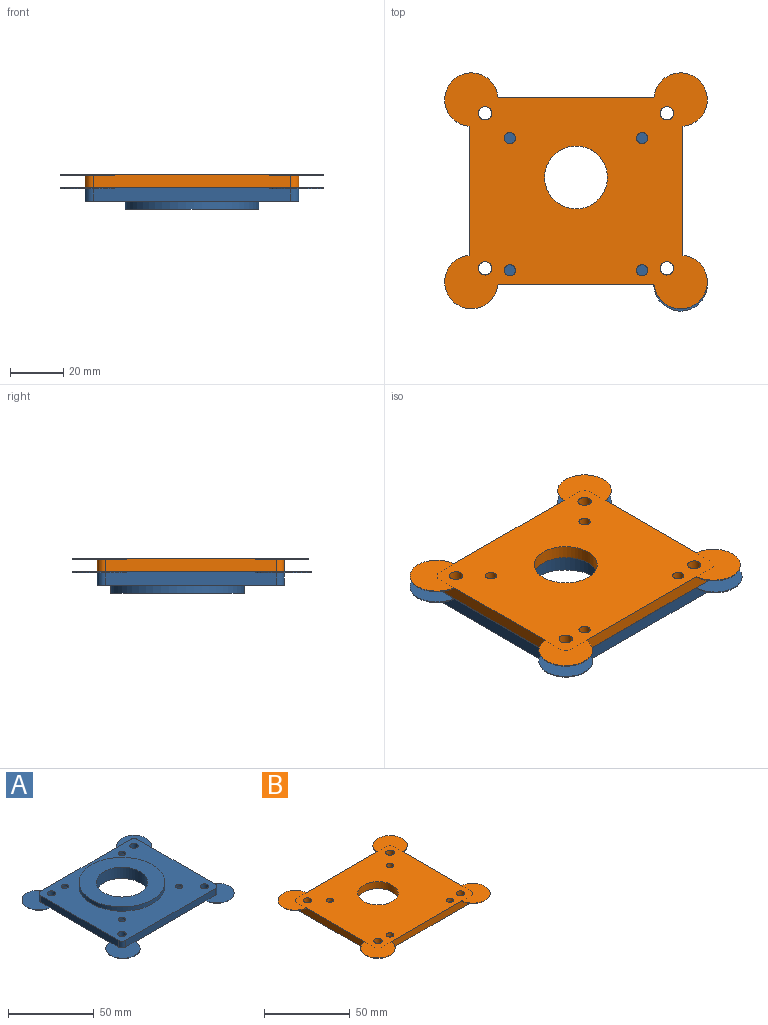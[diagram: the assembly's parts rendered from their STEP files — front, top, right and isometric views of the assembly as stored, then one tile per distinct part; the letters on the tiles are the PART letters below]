
ASSEMBLY  parts=2 mates=1
PART A: 37 faces, bbox 98.2x89.1x8 mm
  f0: cylinder r=3mm len=4.7mm, axis (0,0,-1), area 22.1mm2, adj f9,f10,f16,f36
  f1: cylinder r=3mm len=4.7mm, axis (0,0,1), area 22.1mm2, adj f8,f10,f16,f34
  f2: cylinder r=3mm len=4.7mm, axis (0,0,1), area 22.1mm2, adj f8,f10,f11,f32
  f3: cylinder r=3mm len=4.7mm, axis (0,0,-1), area 22.1mm2, adj f9,f10,f11,f30
  f4: cylinder r=2.1mm len=4.2mm, axis (0,0,1), area 21.1mm2, adj f10,f27
  f5: cylinder r=2.1mm len=4.2mm, axis (0,0,1), area 21.1mm2, adj f10,f28
  f6: cylinder r=2.1mm len=4.2mm, axis (0,0,1), area 21.1mm2, adj f10,f25
  f7: cylinder r=2.1mm len=4.2mm, axis (0,0,1), area 21.1mm2, adj f10,f26
  f8: plane 64x5mm, normal (1,0,0), area 315.3mm2, adj f1,f2,f10,f13,f31,f32,f33,f34
  f9: plane 64x5mm, normal (-1,0,0), area 315.6mm2, adj f0,f3,f10,f13,f29,f30,f35,f36
  f10: plane 80x70mm, normal (0,0,1), area 3494.8mm2, adj f0,f1,f2,f3,f4,f5,f6,f7
  f11: plane 74x5mm, normal (0,-1,0), area 365.3mm2, adj f2,f3,f10,f13,f29,f30,f31,f32
  f12: cylinder r=15mm len=30mm, axis (0,0,-1), area 754mm2, adj f13,f15
  f13: plane 98.24x89.12mm, normal (0,0,-1), area 5379.2mm2, adj f8,f9,f11,f12,f16,f17,f18,f19
  f14: cylinder r=25mm len=50mm, axis (0,0,-1), area 471.2mm2, adj f10,f15
  f15: plane 50x50mm, normal (0,0,1), area 1256.6mm2, adj f12,f14
  f16: plane 74x5mm, normal (0,1,0), area 365.3mm2, adj f0,f1,f10,f13,f33,f34,f35,f36
  f17: cylinder r=2.5mm len=5mm, axis (0,0,-1), area 78.5mm2, adj f10,f13
  f18: cylinder r=2.5mm len=5mm, axis (0,0,-1), area 78.5mm2, adj f10,f13
  f19: cylinder r=2.5mm len=5mm, axis (0,0,-1), area 78.5mm2, adj f10,f13
  f20: cylinder r=2.5mm len=5mm, axis (0,0,-1), area 78.5mm2, adj f10,f13
  f21: cylinder r=5mm len=10mm, axis (0,0,-1), area 15.7mm2, adj f13,f26
  f22: cylinder r=5mm len=10mm, axis (0,0,-1), area 15.7mm2, adj f13,f25
  f23: cylinder r=5mm len=10mm, axis (0,0,-1), area 15.7mm2, adj f13,f28
  f24: cylinder r=5mm len=10mm, axis (0,0,-1), area 15.7mm2, adj f13,f27
  f25: cone r=5.1mm half-angle=45deg, axis (0,0,-1), area 91.5mm2, adj f6,f22
  f26: cone r=5.1mm half-angle=45deg, axis (0,0,-1), area 91.5mm2, adj f7,f21
  f27: cone r=5.1mm half-angle=45deg, axis (0,0,-1), area 91.5mm2, adj f4,f24
  f28: cone r=5.1mm half-angle=45deg, axis (0,0,-1), area 91.5mm2, adj f5,f23
  f29: cylinder r=10mm len=20mm, axis (0,0,-1), area 13.9mm2, adj f9,f11,f13,f30
  f30: plane 20x19.96mm, normal (0,0,1), area 228.8mm2, adj f3,f9,f11,f29
  f31: cylinder r=10mm len=19.96mm, axis (0,0,-1), area 13.6mm2, adj f8,f11,f13,f32
  f32: plane 19.96x19.96mm, normal (0,0,1), area 219.2mm2, adj f2,f8,f11,f31
  f33: cylinder r=10mm len=19.96mm, axis (0,0,-1), area 13.6mm2, adj f8,f13,f16,f34
  f34: plane 19.96x19.96mm, normal (0,0,1), area 219.2mm2, adj f1,f8,f16,f33
  f35: cylinder r=10mm len=19.96mm, axis (0,0,-1), area 13.6mm2, adj f9,f13,f16,f36
  f36: plane 19.96x19.96mm, normal (0,0,1), area 219.2mm2, adj f0,f9,f16,f35
PART B: 35 faces, bbox 98.2x88.2x5 mm
  f0: cylinder r=3mm len=4.7mm, axis (0,0,1), area 22.1mm2, adj f9,f11,f14,f34
  f1: cylinder r=3mm len=4.7mm, axis (0,0,-1), area 22.1mm2, adj f8,f11,f14,f32
  f2: cylinder r=3mm len=4.7mm, axis (0,0,-1), area 22.1mm2, adj f8,f11,f12,f30
  f3: cylinder r=3mm len=4.7mm, axis (0,0,1), area 22.1mm2, adj f9,f11,f12,f28
  f4: cylinder r=2.1mm len=4.2mm, axis (0,0,-1), area 34.3mm2, adj f10,f25
  f5: cylinder r=2.1mm len=4.2mm, axis (0,0,-1), area 34.3mm2, adj f10,f23
  f6: cylinder r=2.1mm len=4.2mm, axis (0,0,-1), area 34.3mm2, adj f10,f26
  f7: cylinder r=2.1mm len=4.2mm, axis (0,0,-1), area 34.3mm2, adj f10,f24
  f8: plane 64x5mm, normal (1,0,0), area 315.3mm2, adj f1,f2,f10,f11,f29,f30,f31,f32
  f9: plane 64x5mm, normal (-1,0,0), area 315.3mm2, adj f0,f3,f10,f11,f27,f28,f33,f34
  f10: plane 98.24x88.24mm, normal (0,0,1), area 5901.5mm2, adj f4,f5,f6,f7,f8,f9,f12,f13
  f11: plane 80x70mm, normal (0,0,-1), area 4878.9mm2, adj f0,f1,f2,f3,f8,f9,f12,f13
  f12: plane 74x5mm, normal (0,1,0), area 365.3mm2, adj f2,f3,f10,f11,f27,f28,f29,f30
  f13: cylinder r=11.75mm len=23.5mm, axis (0,0,-1), area 369.1mm2, adj f10,f11
  f14: plane 74x5mm, normal (0,-1,0), area 365.3mm2, adj f0,f1,f10,f11,f31,f32,f33,f34
  f15: cylinder r=2.5mm len=5mm, axis (0,0,-1), area 78.5mm2, adj f10,f11
  f16: cylinder r=2.5mm len=5mm, axis (0,0,-1), area 78.5mm2, adj f10,f11
  f17: cylinder r=2.5mm len=5mm, axis (0,0,-1), area 78.5mm2, adj f10,f11
  f18: cylinder r=2.5mm len=5mm, axis (0,0,-1), area 78.5mm2, adj f10,f11
  f19: cylinder r=4mm len=8mm, axis (0,0,-1), area 12.6mm2, adj f11,f24
  f20: cylinder r=4mm len=8mm, axis (0,0,-1), area 12.6mm2, adj f11,f26
  f21: cylinder r=4mm len=8mm, axis (0,0,-1), area 12.6mm2, adj f11,f23
  f22: cylinder r=4mm len=8mm, axis (0,0,-1), area 12.6mm2, adj f11,f25
  f23: cone r=2.1mm half-angle=45deg, axis (0,0,-1), area 51.5mm2, adj f5,f21
  f24: cone r=2.1mm half-angle=45deg, axis (0,0,-1), area 51.5mm2, adj f7,f19
  f25: cone r=2.1mm half-angle=45deg, axis (0,0,-1), area 51.5mm2, adj f4,f22
  f26: cone r=2.1mm half-angle=45deg, axis (0,0,-1), area 51.5mm2, adj f6,f20
  f27: cylinder r=10mm len=19.96mm, axis (0,0,1), area 13.6mm2, adj f9,f10,f12,f28
  f28: plane 19.96x19.96mm, normal (0,0,-1), area 219.2mm2, adj f3,f9,f12,f27
  f29: cylinder r=10mm len=19.96mm, axis (0,0,1), area 13.6mm2, adj f8,f10,f12,f30
  f30: plane 19.96x19.96mm, normal (0,0,-1), area 219.2mm2, adj f2,f8,f12,f29
  f31: cylinder r=10mm len=19.96mm, axis (0,0,1), area 13.6mm2, adj f8,f10,f14,f32
  f32: plane 19.96x19.96mm, normal (0,0,-1), area 219.2mm2, adj f1,f8,f14,f31
  f33: cylinder r=10mm len=19.96mm, axis (0,0,1), area 13.6mm2, adj f9,f10,f14,f34
  f34: plane 19.96x19.96mm, normal (0,0,-1), area 219.2mm2, adj f0,f9,f14,f33
PLACE A rot(axis=(0,-1,0),180deg) t=(55.36,-12.29,1.32)mm
PLACE B rot(axis=(0,1,0),0deg) t=(55.36,-22.29,1.32)mm
MATE fastened B.f13 <-> A.f12  axis (0,0,-1) through (55.36,-12.29,1.32)mm
